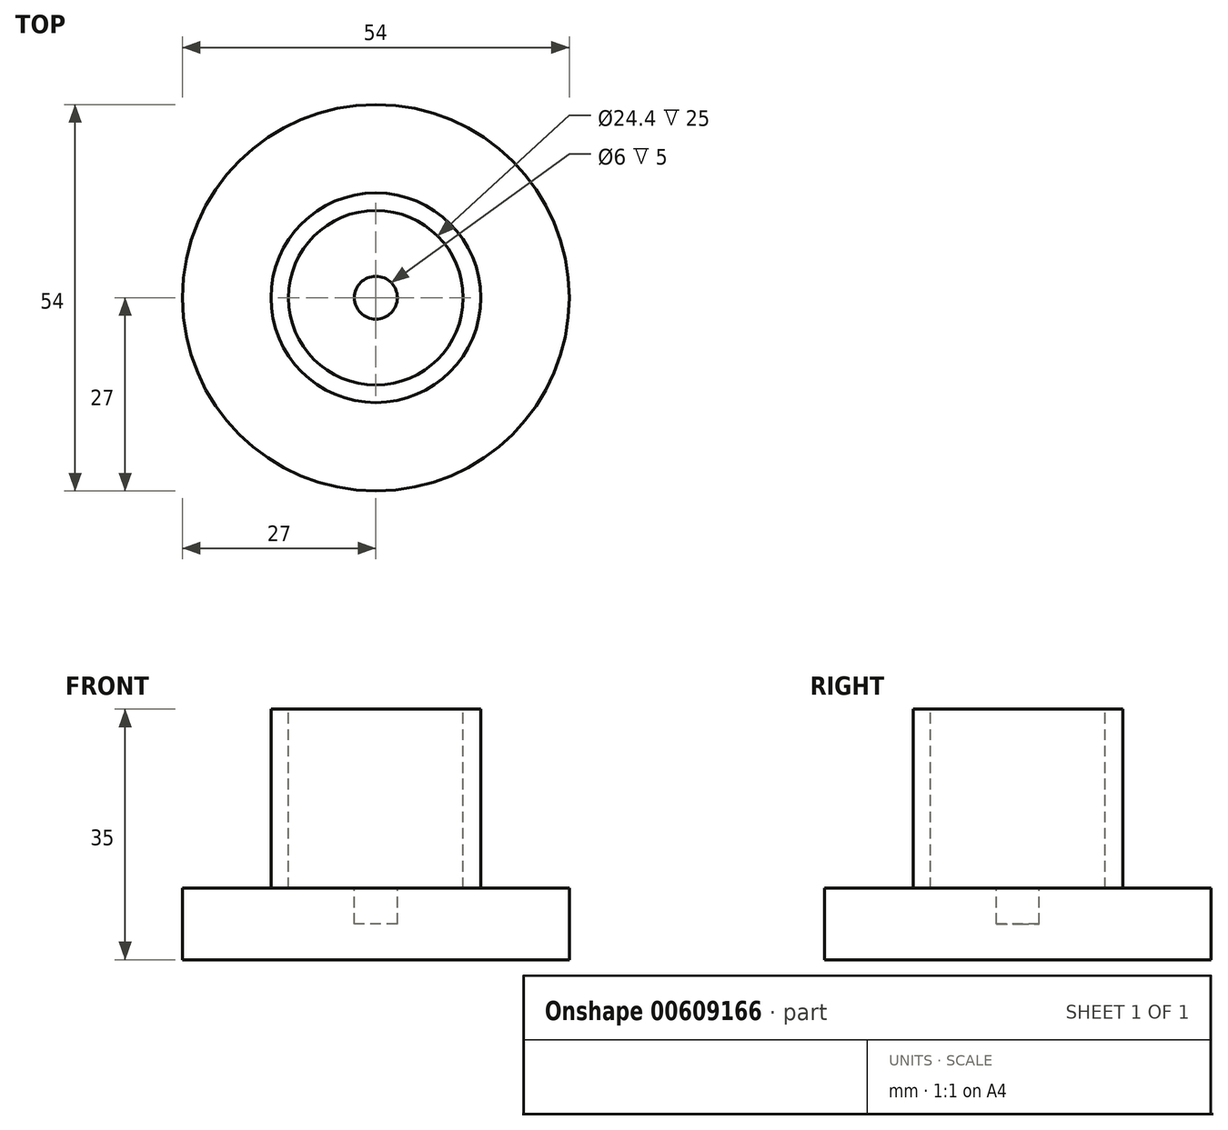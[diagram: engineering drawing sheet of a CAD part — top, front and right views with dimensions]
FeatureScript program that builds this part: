
annotation { "Feature Type Name" : "Feature", "Feature Type Description" : "" }
export const myFeature = defineFeature(function(context is Context, id is Id, definition is map)
    precondition{}
    {
        {
            var Q0;
            Q0=qCreatedBy(makeId("Top.planeOp"),FACE);
            var sketch = newSketch(context, id + "F0", { "sketchPlane" : qUnion([Q0])});
            skCircle(sketch, "E0", {"center": v(0, 0) * mm, "radius": 27 * mm});
            skSolve(sketch);
        }
        {
            var Q0;
            Q0 = qSketchRegion(id + "F0", true);
            extrude(context, id + "F1", {"entities" : qUnion([Q0]), "depth" : 10 * mm, "offsetDistance" : 25 * mm});
        }
        {
            var Q0;
            Q0=makeQuery(id+"F1.opExtrude","CAP_FACE",FACE,{"disambiguationData":[OSD([sQuery(id+"F0.wireOp",EDGE,"E0")])],"isStart":false});
            var sketch = newSketch(context, id + "F2", { "sketchPlane" : qUnion([Q0])});
            skCircle(sketch, "E1", {"center": v(0, 0) * mm, "radius": 14.65 * mm});
            skSolve(sketch);
        }
        {
            var Q0;
            Q0 = qSketchRegion(id + "F2", true);
            extrude(context, id + "F3", {"entities" : qUnion([Q0]), "operationType" : NewBodyOperationType.ADD, "depth" : 25 * mm, "offsetDistance" : 25 * mm});
        }
        {
            var Q0;
            Q0=makeQuery(id+"F3.opExtrude","CAP_FACE",FACE,{"disambiguationData":[OSD([sQuery(id+"F2.wireOp",EDGE,"E1")])],"isStart":false});
            var sketch = newSketch(context, id + "F4", { "sketchPlane" : qUnion([Q0])});
            skCircle(sketch, "E2", {"center": v(0, 0) * mm, "radius": 12.2 * mm});
            skSolve(sketch);
        }
        {
            var Q0;
            Q0 = qSketchRegion(id + "F4", true);
            extrude(context, id + "F5", {"entities" : qUnion([Q0]), "operationType" : NewBodyOperationType.REMOVE, "oppositeDirection" : true, "depth" : 25 * mm, "offsetDistance" : 25 * mm});
        }
        {
            var Q0;
            Q0=makeQuery(id+"F5.boolean.opBoolean","COPY",FACE,{"derivedFrom":makeQuery(id+"F5.opExtrude","CAP_FACE",FACE,{"disambiguationData":[OSD([sQuery(id+"F4.wireOp",EDGE,"E2")])],"isStart":false})});
            var sketch = newSketch(context, id + "F6", { "sketchPlane" : qUnion([Q0])});
            skCircle(sketch, "E3", {"center": v(0, 0) * mm, "radius": 3 * mm});
            skSolve(sketch);
        }
        {
            var Q0;
            Q0 = qSketchRegion(id + "F6", true);
            extrude(context, id + "F7", {"entities" : qUnion([Q0]), "operationType" : NewBodyOperationType.REMOVE, "oppositeDirection" : true, "depth" : 5 * mm, "offsetDistance" : 25 * mm});
        }
    });
